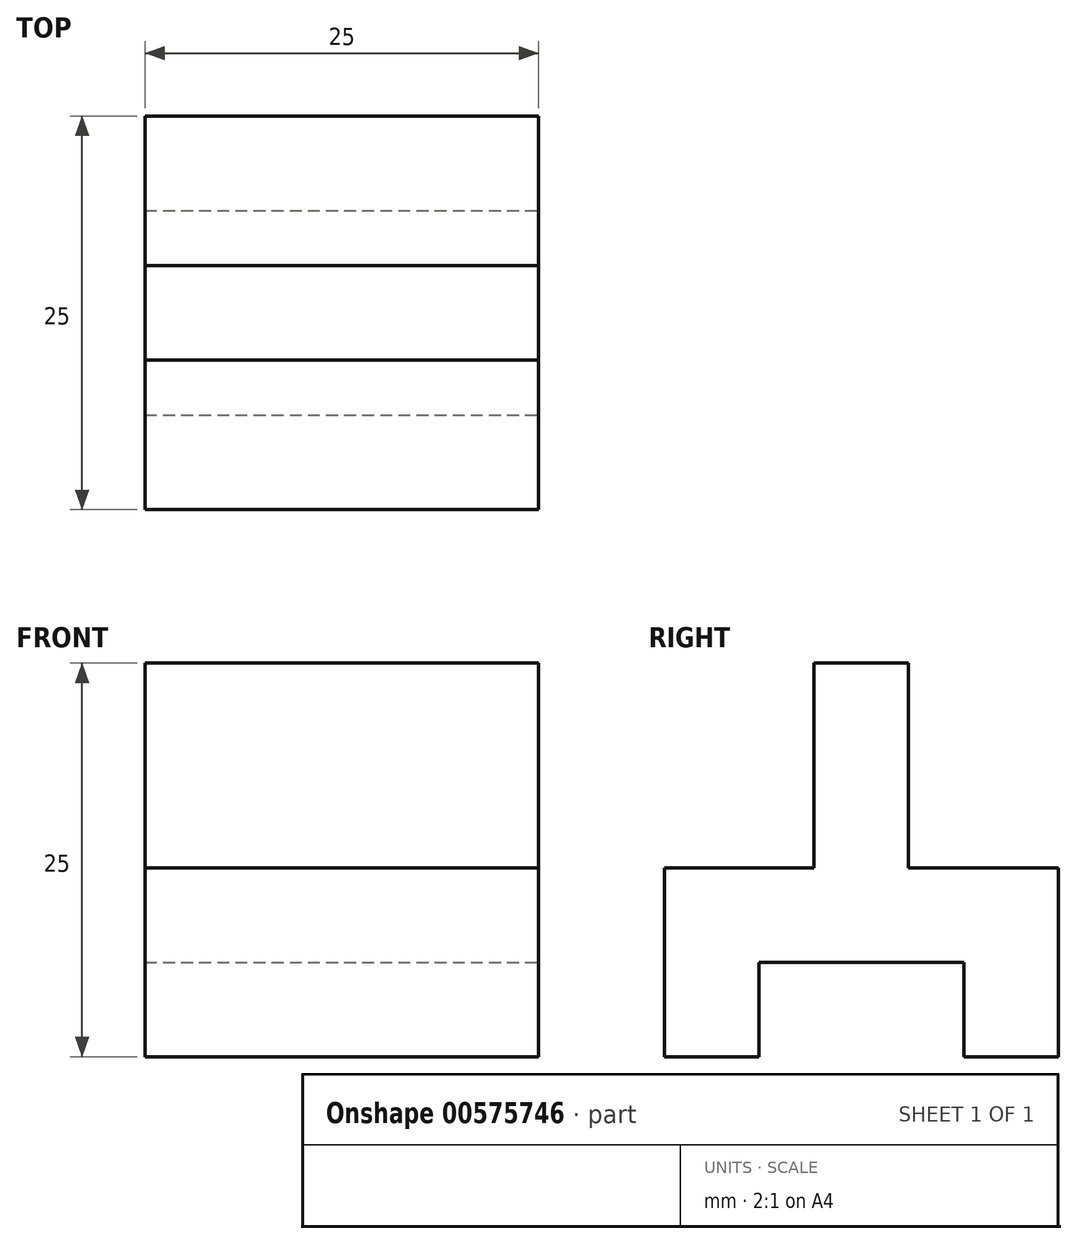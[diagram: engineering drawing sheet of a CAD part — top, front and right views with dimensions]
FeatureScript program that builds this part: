
annotation { "Feature Type Name" : "Feature", "Feature Type Description" : "" }
export const myFeature = defineFeature(function(context is Context, id is Id, definition is map)
    precondition{}
    {
        {
            var Q0;
            Q0=qCreatedBy(makeId("Right.planeOp"),FACE);
            var sketch = newSketch(context, id + "F0", { "sketchPlane" : qUnion([Q0])});
            skLineSegment(sketch, "E0", {"start": v(-3, 0) * mm, "end": v(-3, 13) * mm});
            skLineSegment(sketch, "E1", {"start": v(-3, 13) * mm, "end": v(3, 13) * mm});
            skLineSegment(sketch, "E2", {"start": v(3, 13) * mm, "end": v(3, 0) * mm});
            skLineSegment(sketch, "E3", {"start": v(3, 0) * mm, "end": v(12.5, 0) * mm});
            skLineSegment(sketch, "E4", {"start": v(12.5, 0) * mm, "end": v(12.5, -12) * mm});
            skLineSegment(sketch, "E5", {"start": v(12.5, -12) * mm, "end": v(6.5, -12) * mm});
            skLineSegment(sketch, "E6", {"start": v(-12.5, -12) * mm, "end": v(-12.5, 0) * mm});
            skLineSegment(sketch, "E7", {"start": v(-12.5, 0) * mm, "end": v(-3, 0) * mm});
            skLineSegment(sketch, "E8", {"start": v(-6.5, -12) * mm, "end": v(-6.5, -6) * mm});
            skLineSegment(sketch, "E9", {"start": v(-6.5, -6) * mm, "end": v(6.5, -6) * mm});
            skLineSegment(sketch, "E10", {"start": v(6.5, -6) * mm, "end": v(6.5, -12) * mm});
            skLineSegment(sketch, "E11.trimOffspring", {"start": v(-6.5, -12) * mm, "end": v(-12.5, -12) * mm});
            skSolve(sketch);
        }
        {
            var Q0;
            Q0=makeQuery(id+"F0.imprint","IMPRINT",FACE,{"disambiguationData":[TD([[makeQuery(id+"F0.imprint","IMPRINT",EDGE,{"derivedFrom":sQuery(id+"F0.wireOp",EDGE,"E0")}),-1.0]])]});
            extrude(context, id + "F1", {"entities" : qUnion([Q0]), "oppositeDirection" : true, "depth" : 25 * mm, "offsetDistance" : 25 * mm});
        }
    });
